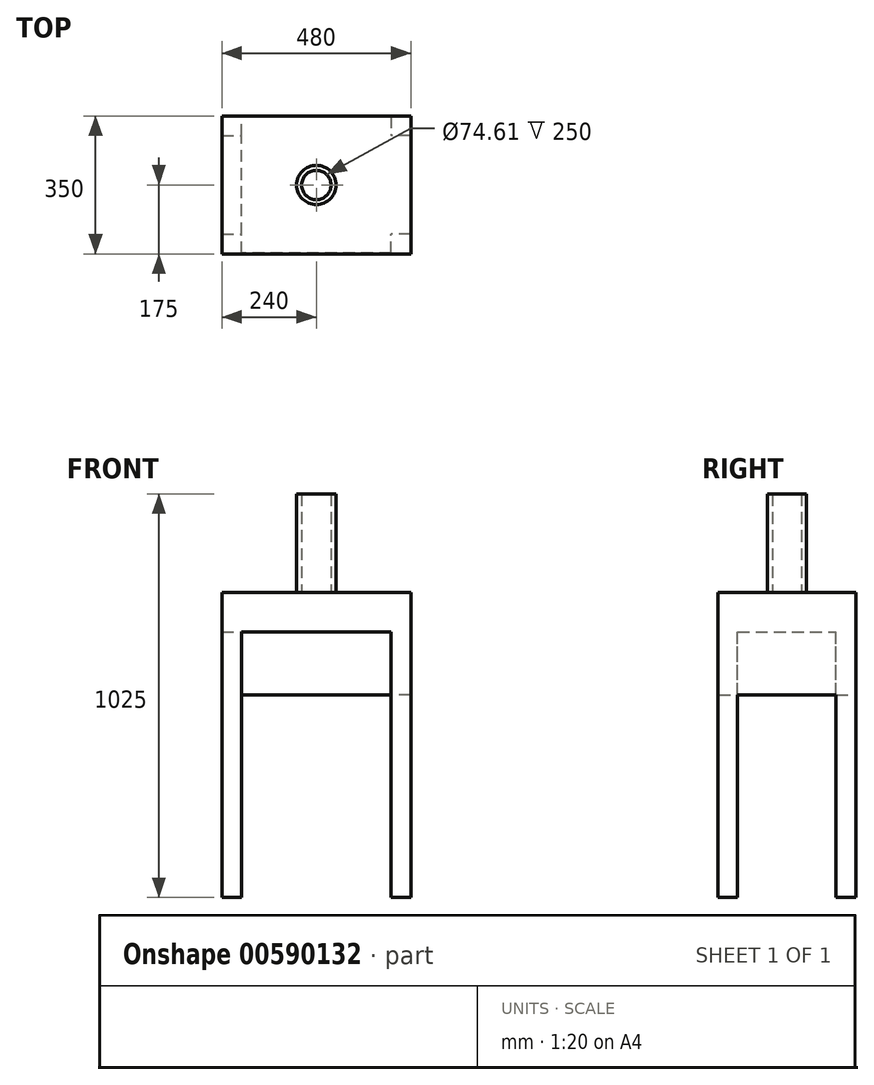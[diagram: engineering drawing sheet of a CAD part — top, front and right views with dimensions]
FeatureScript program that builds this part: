
annotation { "Feature Type Name" : "Feature", "Feature Type Description" : "" }
export const myFeature = defineFeature(function(context is Context, id is Id, definition is map)
    precondition{}
    {
        {
            var Q0;
            Q0=qCreatedBy(makeId("Top.planeOp"),FACE);
            var sketch = newSketch(context, id + "F0", { "sketchPlane" : qUnion([Q0])});
            skPoint(sketch, "E0.middle", {"position": v(0, 0) * mm});
            skPoint(sketch, "E1.middle", {"position": v(241.78, 165.47) * mm});
            skLineSegment(sketch, "E2.bottom", {"start": v(-240, 175) * mm, "end": v(240, 175) * mm});
            skLineSegment(sketch, "E2.top", {"start": v(-240, -175) * mm, "end": v(240, -175) * mm});
            skLineSegment(sketch, "E2.left", {"start": v(-240, 175) * mm, "end": v(-240, -175) * mm});
            skLineSegment(sketch, "E2.right", {"start": v(240, 175) * mm, "end": v(240, -175) * mm});
            skPoint(sketch, "E3.middle", {"position": v(-255.5, 0) * mm});
            skPoint(sketch, "E4.middle", {"position": v(-268.4, -35.37) * mm});
            skSolve(sketch);
        }
        {
            var Q0;
            Q0=makeQuery(id+"F0.imprint","IMPRINT",FACE,{"disambiguationData":[TD([[makeQuery(id+"F0.imprint","IMPRINT",EDGE,{"derivedFrom":sQuery(id+"F0.wireOp",EDGE,"E2.bottom")}),-1.0]])]});
            extrude(context, id + "F1", {"entities" : qUnion([Q0]), "depth" : 100 * mm, "offsetDistance" : 25 * mm});
        }
        {
            var Q0;
            Q0=makeQuery(id+"F1.opExtrude","CAP_FACE",FACE,{"disambiguationData":[OSD([sQuery(id+"F0.wireOp",EDGE,"E2.bottom"),sQuery(id+"F0.wireOp",EDGE,"E2.top"),sQuery(id+"F0.wireOp",EDGE,"E2.left"),sQuery(id+"F0.wireOp",EDGE,"E2.right")])],"isStart":true});
            var sketch = newSketch(context, id + "F2", { "sketchPlane" : qUnion([Q0])});
            skLineSegment(sketch, "E5.bottom", {"start": v(240, 175) * mm, "end": v(190, 175) * mm});
            skLineSegment(sketch, "E5.top", {"start": v(240, 125) * mm, "end": v(190, 125) * mm});
            skLineSegment(sketch, "E5.left", {"start": v(240, 175) * mm, "end": v(240, 125) * mm});
            skLineSegment(sketch, "E5.right", {"start": v(190, 175) * mm, "end": v(190, 125) * mm});
            skSolve(sketch);
        }
        {
            var Q0;
            Q0=makeQuery(id+"F2.imprint","IMPRINT",FACE,{"disambiguationData":[TD([[makeQuery(id+"F2.imprint","IMPRINT",EDGE,{"derivedFrom":sQuery(id+"F2.wireOp",EDGE,"E5.bottom")}),-1.0]])]});
            extrude(context, id + "F3", {"entities" : qUnion([Q0]), "operationType" : NewBodyOperationType.ADD, "depth" : 675 * mm, "offsetDistance" : 25 * mm});
        }
        {
            var Q0;
            Q0=makeQuery(id+"F1.opExtrude","CAP_FACE",FACE,{"disambiguationData":[OSD([sQuery(id+"F0.wireOp",EDGE,"E2.bottom"),sQuery(id+"F0.wireOp",EDGE,"E2.top"),sQuery(id+"F0.wireOp",EDGE,"E2.left"),sQuery(id+"F0.wireOp",EDGE,"E2.right")])],"isStart":true});
            var sketch = newSketch(context, id + "F4", { "sketchPlane" : qUnion([Q0])});
            skLineSegment(sketch, "E6.bottom", {"start": v(240, -175) * mm, "end": v(190, -175) * mm});
            skLineSegment(sketch, "E6.top", {"start": v(240, -125) * mm, "end": v(190, -125) * mm});
            skLineSegment(sketch, "E6.left", {"start": v(240, -175) * mm, "end": v(240, -125) * mm});
            skLineSegment(sketch, "E6.right", {"start": v(190, -175) * mm, "end": v(190, -125) * mm});
            skSolve(sketch);
        }
        {
            var Q0;
            Q0 = qSketchRegion(id + "F4", true);
            extrude(context, id + "F5", {"entities" : qUnion([Q0]), "operationType" : NewBodyOperationType.ADD, "depth" : 675 * mm, "offsetDistance" : 25 * mm});
        }
        {
            var Q0;
            Q0=makeQuery(id+"F1.opExtrude","CAP_FACE",FACE,{"disambiguationData":[OSD([sQuery(id+"F0.wireOp",EDGE,"E2.bottom"),sQuery(id+"F0.wireOp",EDGE,"E2.top"),sQuery(id+"F0.wireOp",EDGE,"E2.left"),sQuery(id+"F0.wireOp",EDGE,"E2.right")])],"isStart":true});
            var sketch = newSketch(context, id + "F6", { "sketchPlane" : qUnion([Q0])});
            skLineSegment(sketch, "E7.bottom", {"start": v(-240, -175) * mm, "end": v(-190, -175) * mm});
            skLineSegment(sketch, "E7.top", {"start": v(-240, -125) * mm, "end": v(-190, -125) * mm});
            skLineSegment(sketch, "E7.left", {"start": v(-240, -175) * mm, "end": v(-240, -125) * mm});
            skLineSegment(sketch, "E7.right", {"start": v(-190, -175) * mm, "end": v(-190, -125) * mm});
            skSolve(sketch);
        }
        {
            var Q0;
            Q0=makeQuery(id+"F6.imprint","IMPRINT",FACE,{"disambiguationData":[TD([[makeQuery(id+"F6.imprint","IMPRINT",EDGE,{"derivedFrom":sQuery(id+"F6.wireOp",EDGE,"E7.bottom")}),1.0]])]});
            extrude(context, id + "F7", {"entities" : qUnion([Q0]), "operationType" : NewBodyOperationType.ADD, "depth" : 675 * mm, "offsetDistance" : 25 * mm});
        }
        {
            var Q0;
            Q0=makeQuery(id+"F1.opExtrude","CAP_FACE",FACE,{"disambiguationData":[OSD([sQuery(id+"F0.wireOp",EDGE,"E2.bottom"),sQuery(id+"F0.wireOp",EDGE,"E2.top"),sQuery(id+"F0.wireOp",EDGE,"E2.left"),sQuery(id+"F0.wireOp",EDGE,"E2.right")])],"isStart":true});
            var sketch = newSketch(context, id + "F8", { "sketchPlane" : qUnion([Q0])});
            skLineSegment(sketch, "E8.bottom", {"start": v(-240, 175) * mm, "end": v(-190, 175) * mm});
            skLineSegment(sketch, "E8.top", {"start": v(-240, 125) * mm, "end": v(-190, 125) * mm});
            skLineSegment(sketch, "E8.left", {"start": v(-240, 175) * mm, "end": v(-240, 125) * mm});
            skLineSegment(sketch, "E8.right", {"start": v(-190, 175) * mm, "end": v(-190, 125) * mm});
            skSolve(sketch);
        }
        {
            var Q0;
            Q0=makeQuery(id+"F8.imprint","IMPRINT",FACE,{"disambiguationData":[TD([[makeQuery(id+"F8.imprint","IMPRINT",EDGE,{"derivedFrom":sQuery(id+"F8.wireOp",EDGE,"E8.bottom")}),-1.0]])]});
            extrude(context, id + "F9", {"entities" : qUnion([Q0]), "operationType" : NewBodyOperationType.ADD, "depth" : 675 * mm, "offsetDistance" : 25 * mm});
        }
        {
            var Q0;
            Q0=makeQuery(id+"F1.opExtrude","CAP_FACE",FACE,{"disambiguationData":[OSD([sQuery(id+"F0.wireOp",EDGE,"E2.bottom"),sQuery(id+"F0.wireOp",EDGE,"E2.top"),sQuery(id+"F0.wireOp",EDGE,"E2.left"),sQuery(id+"F0.wireOp",EDGE,"E2.right")])],"isStart":false});
            var sketch = newSketch(context, id + "F10", { "sketchPlane" : qUnion([Q0])});
            skCircle(sketch, "E9", {"center": v(0, 0) * mm, "radius": 50 * mm});
            skCircle(sketch, "E10", {"center": v(0, 0) * mm, "radius": 37.3 * mm});
            skSolve(sketch);
        }
        {
            var Q0;
            Q0=makeQuery(id+"F10.imprint","IMPRINT",FACE,{"disambiguationData":[TD([[makeQuery(id+"F10.imprint","IMPRINT",EDGE,{"derivedFrom":sQuery(id+"F10.wireOp",EDGE,"E9")}),1.0]])]});
            var Q1;
            Q1 = qSketchRegion(id + "FjkyvlSStwFpssh_1", true);
            extrude(context, id + "F11", {"entities" : qUnion([Q0, Q1]), "operationType" : NewBodyOperationType.ADD, "depth" : 250 * mm, "offsetDistance" : 25 * mm});
        }
        {
            var Q0;
            Q0=makeQuery(id+"F1.opExtrude","CAP_FACE",FACE,{"disambiguationData":[OSD([sQuery(id+"F0.wireOp",EDGE,"E2.bottom"),sQuery(id+"F0.wireOp",EDGE,"E2.top"),sQuery(id+"F0.wireOp",EDGE,"E2.left"),sQuery(id+"F0.wireOp",EDGE,"E2.right")])],"isStart":true});
            var sketch = newSketch(context, id + "F12", { "sketchPlane" : qUnion([Q0])});
            skLineSegment(sketch, "E11.bottom", {"start": v(0, -41.96) * mm, "end": v(-10.36, -41.96) * mm});
            skLineSegment(sketch, "E11.top", {"start": v(0, 0) * mm, "end": v(-10.36, 0) * mm});
            skLineSegment(sketch, "E11.left", {"start": v(0, -41.96) * mm, "end": v(0, 0) * mm});
            skLineSegment(sketch, "E11.right", {"start": v(-10.36, -41.96) * mm, "end": v(-10.36, 0) * mm});
            skSolve(sketch);
        }
        {
            var Q0;
            Q0=sQuery(id+"F12.wireOp",EDGE,"E11.left");
            var Q1;
            Q1 = qBodyType(qCreatedBy(id + "F12" ,EDGE), BodyType.WIRE);
            extrude(context, id + "F13", {"bodyType" : ToolBodyType.SURFACE, "surfaceEntities" : qUnion([Q0, Q1]), "depth" : 100 * mm, "offsetDistance" : 25 * mm});
        }
        {
            var Q0;
            Q0=makeQuery(id+"F1.opExtrude","CAP_FACE",FACE,{"disambiguationData":[OSD([sQuery(id+"F0.wireOp",EDGE,"E2.bottom"),sQuery(id+"F0.wireOp",EDGE,"E2.top"),sQuery(id+"F0.wireOp",EDGE,"E2.left"),sQuery(id+"F0.wireOp",EDGE,"E2.right")])],"isStart":true});
            var sketch = newSketch(context, id + "F14", { "sketchPlane" : qUnion([Q0])});
            skLineSegment(sketch, "E12.bottom", {"start": v(240, -35.88) * mm, "end": v(-190, -35.88) * mm});
            skLineSegment(sketch, "E12.top", {"start": v(240, -175) * mm, "end": v(-190, -175) * mm});
            skLineSegment(sketch, "E12.left", {"start": v(240, -35.88) * mm, "end": v(240, -175) * mm});
            skLineSegment(sketch, "E12.right", {"start": v(-190, -35.88) * mm, "end": v(-190, -175) * mm});
            skSolve(sketch);
        }
        {
            var Q0;
            Q0 = qSketchRegion(id + "F14", true);
            extrude(context, id + "F15", {"entities" : qUnion([Q0]), "operationType" : NewBodyOperationType.ADD, "depth" : 160 * mm, "offsetDistance" : 25 * mm});
        }
        {
            var Q0;
            Q0=makeQuery(id+"F15.opExtrude","SWEPT_FACE",FACE,{"disambiguationData":[OSD([sQuery(id+"F14.wireOp",EDGE,"E12.bottom")])]});
            extrude(context, id + "F16", {"entities" : qUnion([Q0]), "operationType" : NewBodyOperationType.ADD, "depth" : 209 * mm, "offsetDistance" : 25 * mm});
        }
        {
            var Q0;
            {var subQ0=sQuery(id+"F14.wireOp",EDGE,"E12.right");Q0=makeQuery(id+"F16.boolean.opBoolean","MERGE",FACE,{"derivedFrom":[makeQuery(id+"F15.opExtrude","SWEPT_FACE",FACE,{"disambiguationData":[OSD([subQ0])]}),makeQuery(id+"F16.opExtrude","SWEPT_FACE",FACE,{"disambiguationData":[OSD([sQuery(id+"F14.wireOp",EDGE,"E12.bottom"),subQ0])]})]});}
            var sketch = newSketch(context, id + "F17", { "sketchPlane" : qUnion([Q0])});
            skLineSegment(sketch, "E13.bottom", {"start": v(-125, 0) * mm, "end": v(-174.9, 0) * mm});
            skLineSegment(sketch, "E13.top", {"start": v(-125, -160) * mm, "end": v(-174.9, -160) * mm});
            skLineSegment(sketch, "E13.left", {"start": v(-125, 0) * mm, "end": v(-125, -160) * mm});
            skLineSegment(sketch, "E13.right", {"start": v(-174.9, 0) * mm, "end": v(-174.9, -160) * mm});
            skSolve(sketch);
        }
        {
            var Q0;
            Q0 = qSketchRegion(id + "F17", true);
            extrude(context, id + "F18", {"entities" : qUnion([Q0]), "operationType" : NewBodyOperationType.ADD, "oppositeDirection" : true, "depth" : 430 * mm, "offsetDistance" : 25 * mm});
        }
    });
